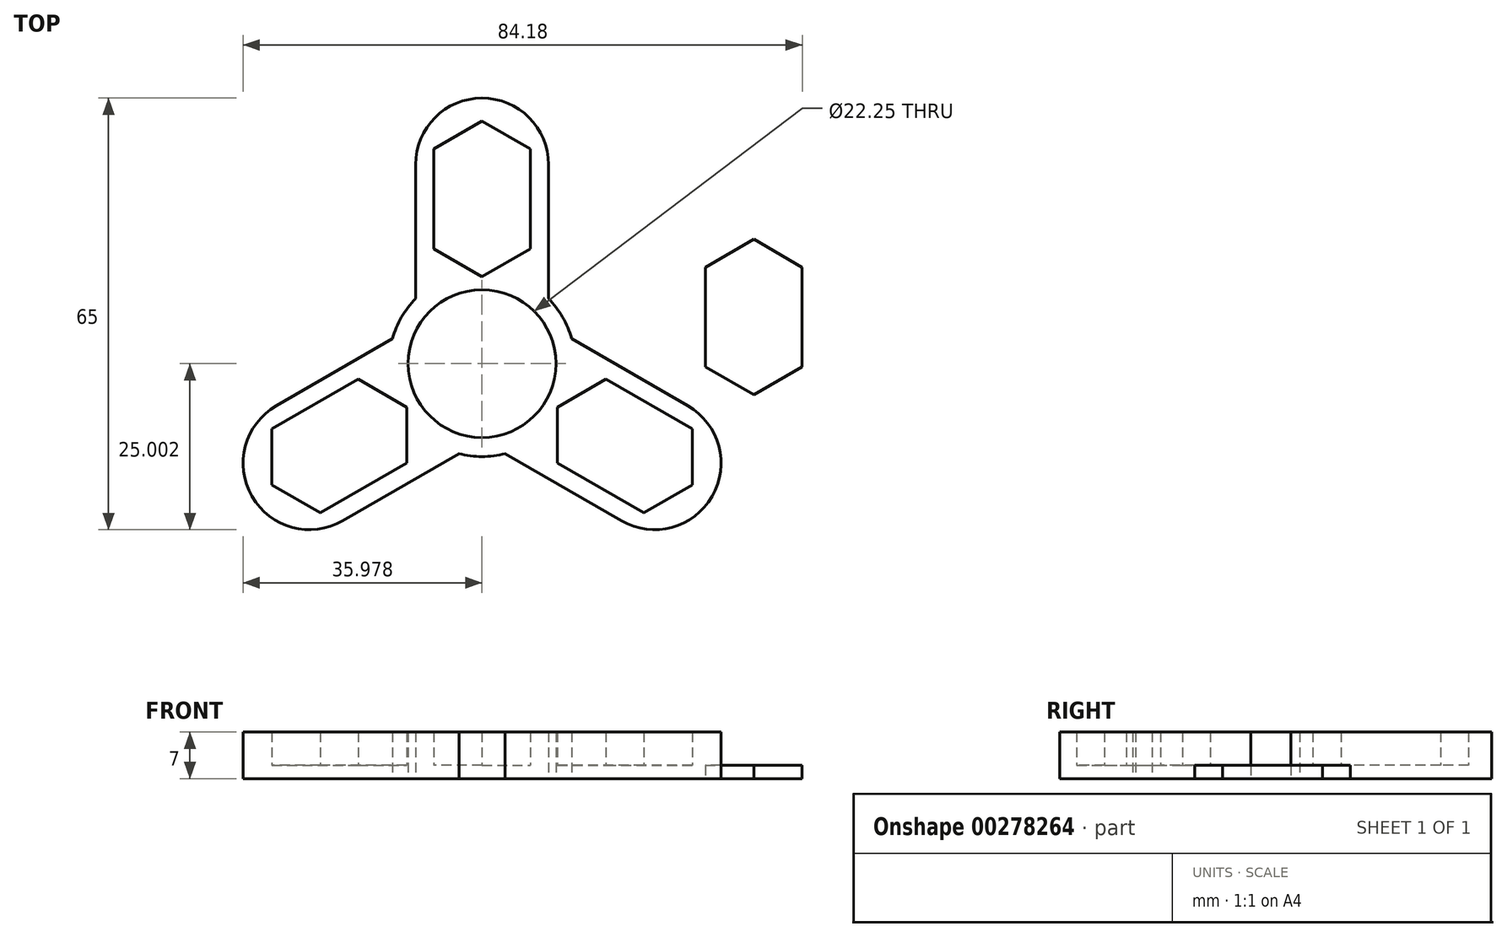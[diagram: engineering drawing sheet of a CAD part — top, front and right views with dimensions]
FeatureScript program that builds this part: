
annotation { "Feature Type Name" : "Feature", "Feature Type Description" : "" }
export const myFeature = defineFeature(function(context is Context, id is Id, definition is map)
    precondition{}
    {
        {
            var Q0;
            Q0=qCreatedBy(makeId("Top.planeOp"),FACE);
            var sketch = newSketch(context, id + "F0", { "sketchPlane" : qUnion([Q0])});
            skPoint(sketch, "E0.center", {"position": v(-54.6, 34) * mm});
            skArc(sketch, "E1", {"start": v(-44.6, 64) * mm, "mid": v(-54.6, 74) * mm, "end": v(-64.6, 64) * mm});
            skPoint(sketch, "E2", {"position": v(-64.6, 64) * mm});
            skPoint(sketch, "E3", {"position": v(-44.6, 64) * mm});
            skLineSegment(sketch, "E4", {"start": v(-64.6, 64) * mm, "end": v(-44.6, 64) * mm});
            skLineSegment(sketch, "E5", {"start": v(-44.6, 64) * mm, "end": v(-44.6, 43.79) * mm});
            skLineSegment(sketch, "E6", {"start": v(-64.6, 64) * mm, "end": v(-64.6, 43.79) * mm});
            skArc(sketch, "E7.2.5", {"start": v(-41.12, 37.75) * mm, "mid": v(-42.48, 41) * mm, "end": v(-44.6, 43.79) * mm});
            skLineSegment(sketch, "E8", {"start": v(-54.6, 74) * mm, "end": v(-54.6, 34) * mm});
            skCircle(sketch, "E9", {"center": v(-54.6, 34) * mm, "radius": 11.12 * mm});
            skLineSegment(sketch, "E10.0", {"start": v(-47.3, 66.32) * mm, "end": v(-47.3, 51.32) * mm});
            skLineSegment(sketch, "E10.1", {"start": v(-47.3, 51.32) * mm, "end": v(-54.6, 47.1) * mm});
            skLineSegment(sketch, "E10.2", {"start": v(-54.6, 47.1) * mm, "end": v(-61.9, 51.32) * mm});
            skLineSegment(sketch, "E10.3", {"start": v(-61.9, 51.32) * mm, "end": v(-61.9, 66.32) * mm});
            skLineSegment(sketch, "E10.4", {"start": v(-61.9, 66.32) * mm, "end": v(-54.6, 70.53) * mm});
            skLineSegment(sketch, "E10.5", {"start": v(-54.6, 70.53) * mm, "end": v(-47.3, 66.32) * mm});
            skPoint(sketch, "E10.0.midPoint", {"position": v(-47.3, 58.82) * mm});
            skLineSegment(sketch, "E11", {"start": v(-61.9, 51.32) * mm, "end": v(-47.3, 51.32) * mm});
            skLineSegment(sketch, "E12.1.0", {"start": v(-73.25, 31.65) * mm, "end": v(-65.96, 27.43) * mm});
            skLineSegment(sketch, "E12.1.1", {"start": v(-86.24, 15.72) * mm, "end": v(-86.24, 24.15) * mm});
            skLineSegment(sketch, "E12.1.2", {"start": v(-89.24, 14) * mm, "end": v(-54.6, 34) * mm});
            skLineSegment(sketch, "E12.1.3", {"start": v(-86.24, 24.15) * mm, "end": v(-73.25, 31.65) * mm});
            skLineSegment(sketch, "E12.1.4", {"start": v(-65.96, 19.01) * mm, "end": v(-78.95, 11.51) * mm});
            skLineSegment(sketch, "E12.1.5", {"start": v(-65.96, 27.43) * mm, "end": v(-65.96, 19.01) * mm});
            skPoint(sketch, "E12.1.6", {"position": v(-79.75, 27.9) * mm});
            skLineSegment(sketch, "E12.1.7", {"start": v(-65.96, 19.01) * mm, "end": v(-73.25, 31.65) * mm});
            skArc(sketch, "E12.1.8", {"start": v(-64.6, 43.79) * mm, "mid": v(-66.73, 41) * mm, "end": v(-68.09, 37.75) * mm});
            skLineSegment(sketch, "E12.1.9", {"start": v(-75.58, 10.33) * mm, "end": v(-85.58, 27.65) * mm});
            skLineSegment(sketch, "E12.1.10", {"start": v(-75.58, 10.33) * mm, "end": v(-58.09, 20.43) * mm});
            skPoint(sketch, "E12.1.11", {"position": v(-85.58, 27.65) * mm});
            skLineSegment(sketch, "E12.1.12", {"start": v(-85.58, 27.65) * mm, "end": v(-68.09, 37.75) * mm});
            skPoint(sketch, "E12.1.13", {"position": v(-75.58, 10.33) * mm});
            skArc(sketch, "E12.1.15", {"start": v(-85.58, 27.65) * mm, "mid": v(-89.24, 14) * mm, "end": v(-75.58, 10.33) * mm});
            skPoint(sketch, "E12.1.16", {"position": v(-80.58, 19) * mm});
            skLineSegment(sketch, "E12.1.18", {"start": v(-78.95, 11.51) * mm, "end": v(-86.24, 15.72) * mm});
            skArc(sketch, "E12.1.20", {"start": v(-64.6, 43.79) * mm, "mid": v(-66.73, 41) * mm, "end": v(-68.09, 37.75) * mm});
            skArc(sketch, "E12.1.22", {"start": v(-64.6, 43.79) * mm, "mid": v(-66.73, 41) * mm, "end": v(-68.09, 37.75) * mm});
            skLineSegment(sketch, "E12.2.0", {"start": v(-43.25, 19.01) * mm, "end": v(-43.25, 27.43) * mm});
            skLineSegment(sketch, "E12.2.1", {"start": v(-22.96, 15.72) * mm, "end": v(-30.26, 11.51) * mm});
            skLineSegment(sketch, "E12.2.2", {"start": v(-19.96, 14) * mm, "end": v(-54.6, 34) * mm});
            skLineSegment(sketch, "E12.2.3", {"start": v(-30.26, 11.51) * mm, "end": v(-43.25, 19.01) * mm});
            skLineSegment(sketch, "E12.2.4", {"start": v(-35.95, 31.65) * mm, "end": v(-22.96, 24.15) * mm});
            skLineSegment(sketch, "E12.2.5", {"start": v(-43.25, 27.43) * mm, "end": v(-35.95, 31.65) * mm});
            skPoint(sketch, "E12.2.6", {"position": v(-36.75, 15.26) * mm});
            skLineSegment(sketch, "E12.2.7", {"start": v(-35.95, 31.65) * mm, "end": v(-43.25, 19.01) * mm});
            skArc(sketch, "E12.2.8", {"start": v(-58.09, 20.43) * mm, "mid": v(-54.6, 20) * mm, "end": v(-51.12, 20.43) * mm});
            skLineSegment(sketch, "E12.2.9", {"start": v(-23.62, 27.65) * mm, "end": v(-33.62, 10.33) * mm});
            skLineSegment(sketch, "E12.2.10", {"start": v(-23.62, 27.65) * mm, "end": v(-41.12, 37.75) * mm});
            skPoint(sketch, "E12.2.11", {"position": v(-33.62, 10.33) * mm});
            skLineSegment(sketch, "E12.2.12", {"start": v(-33.62, 10.33) * mm, "end": v(-51.12, 20.43) * mm});
            skPoint(sketch, "E12.2.13", {"position": v(-23.62, 27.65) * mm});
            skArc(sketch, "E12.2.15", {"start": v(-33.62, 10.33) * mm, "mid": v(-19.96, 14) * mm, "end": v(-23.62, 27.65) * mm});
            skPoint(sketch, "E12.2.16", {"position": v(-28.62, 19) * mm});
            skLineSegment(sketch, "E12.2.18", {"start": v(-22.96, 24.15) * mm, "end": v(-22.96, 15.72) * mm});
            skArc(sketch, "E12.2.20", {"start": v(-58.09, 20.43) * mm, "mid": v(-54.6, 20) * mm, "end": v(-51.12, 20.43) * mm});
            skArc(sketch, "E12.2.22", {"start": v(-58.09, 20.43) * mm, "mid": v(-54.6, 20) * mm, "end": v(-51.12, 20.43) * mm});
            skSolve(sketch);
        }
        {
            var Q0;
            {var subQ3=sQuery(id+"F0.wireOp",EDGE,"E10.5");Q0=makeQuery(id+"F0.imprint","IMPRINT",FACE,{"disambiguationData":[TD([[makeQuery(id+"F0.imprint","IMPRINT",EDGE,{"derivedFrom":subQ3}),1.0]])]});}
            var sketch = newSketch(context, id + "F1", { "sketchPlane" : qUnion([Q0])});
            skLineSegment(sketch, "E13.0", {"start": v(-6.4, 48.5) * mm, "end": v(-6.4, 33.5) * mm});
            skLineSegment(sketch, "E13.1", {"start": v(-6.4, 33.5) * mm, "end": v(-13.7, 29.3) * mm});
            skLineSegment(sketch, "E13.2", {"start": v(-13.7, 29.3) * mm, "end": v(-21, 33.5) * mm});
            skLineSegment(sketch, "E13.3", {"start": v(-21, 33.5) * mm, "end": v(-21, 48.5) * mm});
            skLineSegment(sketch, "E13.4", {"start": v(-21, 48.5) * mm, "end": v(-13.7, 52.72) * mm});
            skLineSegment(sketch, "E13.5", {"start": v(-13.7, 52.72) * mm, "end": v(-6.4, 48.5) * mm});
            skSolve(sketch);
        }
        {
            var Q0;
            Q0 = qSketchRegion(id + "F0", true);
            var Q1;
            Q1=sQuery(id+"F1.wireOp",EDGE,"E13.0");
            var Q2;
            Q2=sQuery(id+"F1.wireOp",EDGE,"E13.5");
            var Q3;
            Q3=sQuery(id+"F1.wireOp",EDGE,"E13.4");
            var Q4;
            Q4=sQuery(id+"F1.wireOp",EDGE,"E13.3");
            var Q5;
            Q5=sQuery(id+"F1.wireOp",EDGE,"E13.2");
            var Q6;
            Q6=sQuery(id+"F1.wireOp",EDGE,"E13.1");
            extrude(context, id + "F2", {"entities" : qUnion([Q0]), "surfaceEntities" : qUnion([Q1, Q2, Q3, Q4, Q5, Q6]), "depth" : 7 * mm, "offsetDistance" : 25 * mm});
        }
        {
            var Q0;
            {var subQ5=sQuery(id+"F0.wireOp",EDGE,"E10.4");Q0=makeQuery(id+"F0.imprint","IMPRINT",FACE,{"disambiguationData":[TD([[makeQuery(id+"F0.imprint","IMPRINT",EDGE,{"derivedFrom":subQ5}),-1.0]])]});}
            var Q1;
            {var subQ5=sQuery(id+"F0.wireOp",EDGE,"E10.5");Q1=makeQuery(id+"F0.imprint","IMPRINT",FACE,{"disambiguationData":[TD([[makeQuery(id+"F0.imprint","IMPRINT",EDGE,{"derivedFrom":subQ5}),-1.0]])]});}
            var Q2;
            {var subQ0=sQuery(id+"F0.wireOp",EDGE,"E8");var subQ1=sQuery(id+"F0.wireOp",EDGE,"E4");var subQ2=makeQuery(id+"F0.imprint","INTERSECT",VERTEX,{"derivedFrom":[subQ1,subQ0]});Q2=makeQuery(id+"F0.imprint","IMPRINT",FACE,{"disambiguationData":[TD([[makeQuery(id+"F0.imprint","IMPRINT",EDGE,{"disambiguationData":[TD([[subQ2,-1.0]])],"derivedFrom":subQ1}),-1.0]])]});}
            var Q3;
            {var subQ0=sQuery(id+"F0.wireOp",EDGE,"E10.3");var subQ1=sQuery(id+"F0.wireOp",EDGE,"E4");var subQ2=makeQuery(id+"F0.imprint","INTERSECT",VERTEX,{"derivedFrom":[subQ1,subQ0]});Q3=makeQuery(id+"F0.imprint","IMPRINT",FACE,{"disambiguationData":[TD([[makeQuery(id+"F0.imprint","IMPRINT",EDGE,{"disambiguationData":[TD([[subQ2,-1.0]])],"derivedFrom":subQ1}),-1.0]])]});}
            var Q4;
            {var subQ0=sQuery(id+"F0.wireOp",EDGE,"E10.1");Q4=makeQuery(id+"F0.imprint","IMPRINT",FACE,{"disambiguationData":[TD([[makeQuery(id+"F0.imprint","IMPRINT",EDGE,{"derivedFrom":subQ0}),-1.0]])]});}
            var Q5;
            {var subQ0=sQuery(id+"F0.wireOp",EDGE,"E10.2");Q5=makeQuery(id+"F0.imprint","IMPRINT",FACE,{"disambiguationData":[TD([[makeQuery(id+"F0.imprint","IMPRINT",EDGE,{"derivedFrom":subQ0}),-1.0]])]});}
            var Q6;
            {var subQ0=sQuery(id+"F0.wireOp",EDGE,"E12.1.9");var subQ1=sQuery(id+"F0.wireOp",EDGE,"E12.1.2");var subQ2=makeQuery(id+"F0.imprint","INTERSECT",VERTEX,{"derivedFrom":[subQ1,subQ0]});Q6=makeQuery(id+"F0.imprint","IMPRINT",FACE,{"disambiguationData":[TD([[makeQuery(id+"F0.imprint","IMPRINT",EDGE,{"disambiguationData":[TD([[subQ2,-1.0]])],"derivedFrom":subQ1}),1.0]])]});}
            var Q7;
            {var subQ0=sQuery(id+"F0.wireOp",EDGE,"E12.1.0");Q7=makeQuery(id+"F0.imprint","IMPRINT",FACE,{"disambiguationData":[TD([[makeQuery(id+"F0.imprint","IMPRINT",EDGE,{"derivedFrom":subQ0}),-1.0]])]});}
            var Q8;
            {var subQ0=sQuery(id+"F0.wireOp",EDGE,"E12.1.5");Q8=makeQuery(id+"F0.imprint","IMPRINT",FACE,{"disambiguationData":[TD([[makeQuery(id+"F0.imprint","IMPRINT",EDGE,{"derivedFrom":subQ0}),-1.0]])]});}
            var Q9;
            {var subQ0=sQuery(id+"F0.wireOp",EDGE,"E12.1.9");var subQ1=sQuery(id+"F0.wireOp",EDGE,"E12.1.2");var subQ2=makeQuery(id+"F0.imprint","INTERSECT",VERTEX,{"derivedFrom":[subQ1,subQ0]});Q9=makeQuery(id+"F0.imprint","IMPRINT",FACE,{"disambiguationData":[TD([[makeQuery(id+"F0.imprint","IMPRINT",EDGE,{"disambiguationData":[TD([[subQ2,-1.0]])],"derivedFrom":subQ1}),-1.0]])]});}
            var Q10;
            {var subQ0=sQuery(id+"F0.wireOp",EDGE,"E12.1.18");Q10=makeQuery(id+"F0.imprint","IMPRINT",FACE,{"disambiguationData":[TD([[makeQuery(id+"F0.imprint","IMPRINT",EDGE,{"derivedFrom":subQ0}),-1.0]])]});}
            var Q11;
            {var subQ0=sQuery(id+"F0.wireOp",EDGE,"E12.1.1");Q11=makeQuery(id+"F0.imprint","IMPRINT",FACE,{"disambiguationData":[TD([[makeQuery(id+"F0.imprint","IMPRINT",EDGE,{"derivedFrom":subQ0}),-1.0]])]});}
            var Q12;
            {var subQ0=sQuery(id+"F0.wireOp",EDGE,"E12.2.9");var subQ1=sQuery(id+"F0.wireOp",EDGE,"E12.2.2");var subQ2=makeQuery(id+"F0.imprint","INTERSECT",VERTEX,{"derivedFrom":[subQ1,subQ0]});Q12=makeQuery(id+"F0.imprint","IMPRINT",FACE,{"disambiguationData":[TD([[makeQuery(id+"F0.imprint","IMPRINT",EDGE,{"disambiguationData":[TD([[subQ2,-1.0]])],"derivedFrom":subQ1}),1.0]])]});}
            var Q13;
            {var subQ0=sQuery(id+"F0.wireOp",EDGE,"E12.2.1");Q13=makeQuery(id+"F0.imprint","IMPRINT",FACE,{"disambiguationData":[TD([[makeQuery(id+"F0.imprint","IMPRINT",EDGE,{"derivedFrom":subQ0}),-1.0]])]});}
            var Q14;
            {var subQ0=sQuery(id+"F0.wireOp",EDGE,"E12.2.18");Q14=makeQuery(id+"F0.imprint","IMPRINT",FACE,{"disambiguationData":[TD([[makeQuery(id+"F0.imprint","IMPRINT",EDGE,{"derivedFrom":subQ0}),-1.0]])]});}
            var Q15;
            {var subQ0=sQuery(id+"F0.wireOp",EDGE,"E12.2.9");var subQ1=sQuery(id+"F0.wireOp",EDGE,"E12.2.2");var subQ2=makeQuery(id+"F0.imprint","INTERSECT",VERTEX,{"derivedFrom":[subQ1,subQ0]});Q15=makeQuery(id+"F0.imprint","IMPRINT",FACE,{"disambiguationData":[TD([[makeQuery(id+"F0.imprint","IMPRINT",EDGE,{"disambiguationData":[TD([[subQ2,-1.0]])],"derivedFrom":subQ1}),-1.0]])]});}
            var Q16;
            {var subQ0=sQuery(id+"F0.wireOp",EDGE,"E12.2.5");Q16=makeQuery(id+"F0.imprint","IMPRINT",FACE,{"disambiguationData":[TD([[makeQuery(id+"F0.imprint","IMPRINT",EDGE,{"derivedFrom":subQ0}),-1.0]])]});}
            var Q17;
            {var subQ0=sQuery(id+"F0.wireOp",EDGE,"E12.2.0");Q17=makeQuery(id+"F0.imprint","IMPRINT",FACE,{"disambiguationData":[TD([[makeQuery(id+"F0.imprint","IMPRINT",EDGE,{"derivedFrom":subQ0}),-1.0]])]});}
            extrude(context, id + "F3", {"entities" : qUnion([Q0, Q1, Q2, Q3, Q4, Q5, Q6, Q7, Q8, Q9, Q10, Q11, Q12, Q13, Q14, Q15, Q16, Q17]), "operationType" : NewBodyOperationType.ADD, "depth" : 2 * mm, "offsetDistance" : 25 * mm});
        }
        {
            var Q0;
            Q0=makeQuery(id+"F1.imprint","IMPRINT",FACE,{"disambiguationData":[TD([[makeQuery(id+"F1.imprint","IMPRINT",EDGE,{"derivedFrom":sQuery(id+"F1.wireOp",EDGE,"E13.0")}),-1.0]])]});
            extrude(context, id + "F4", {"entities" : qUnion([Q0]), "depth" : 2 * mm, "offsetDistance" : 25 * mm});
        }
    });
